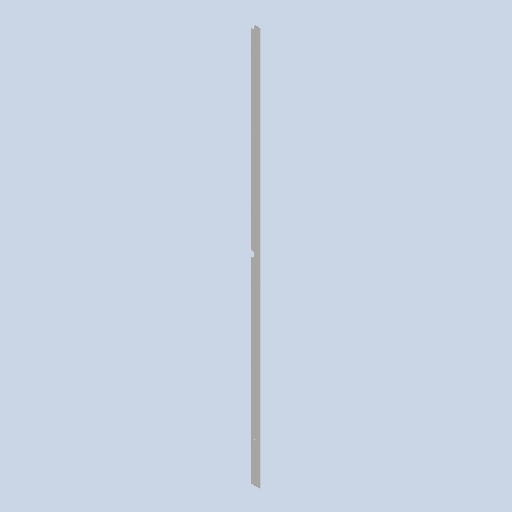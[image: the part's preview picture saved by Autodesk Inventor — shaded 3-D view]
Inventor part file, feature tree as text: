
AUTODESK INVENTOR PART (.ipt)
format: ipt  version: 2025 (Build 290162010, 162A)  size: 323,584 bytes
history: native  units: mm
features: other x4, sketch x4, projected_geometry x3, extrude x2, pattern_linear x2, sheet_metal_op x1
ambient origin geometry x8: Origin, YZ Plane, XZ Plane, XY Plane, X Axis, Y Axis, Z Axis, Center Point
bodies: Body1 (feature_tree)
feature tree (16):
  sheet_metal_op  "Face2"
  other  "Mark1"
  extrude  "Extrusion2"  Depth=2980.0mm
  pattern_linear  "Rectangular Pattern1"  Spacing1=0.0mm  [1 undecoded]
  extrude  "Extrusion3"  Depth=10.0mm
  pattern_linear  "Rectangular Pattern2"  Count1=5  [1 undecoded]
  other  "Corner Chamfer1"
  sketch  "Sketch6"  dims[d26=70.28909mm d27=2980.0mm]
  other  "Plate4"
  sketch  "Sketch7"  dims[d28=3.0mm]
  projected_geometry  "Projected Loop1"
  sketch  "Sketch8"  dims[d29=36.144545mm]
  projected_geometry  "Projected Loop2"
  sketch  "Sketch9"  dims[d30=3.2mm d32=0.0mm d33=0.0mm d34=60.0mm d36=500.0mm d37=50.0mm d38=1490.0mm d39=0.0mm d40=0.0mm d41=20.0mm d43=1480.0mm d44=200.0mm d45=15.0mm d47=10.0mm d48=6.0mm d49=6.0mm d50=45.0deg d51=182.0mm]
  projected_geometry  "Projected Loop3"
  other  "Definition1"
note: 2 required parameter values undecoded (feature->parameter linkage not recoverable at this tier; creation-order binding heuristic only, values carry confidence <= 0.55)
